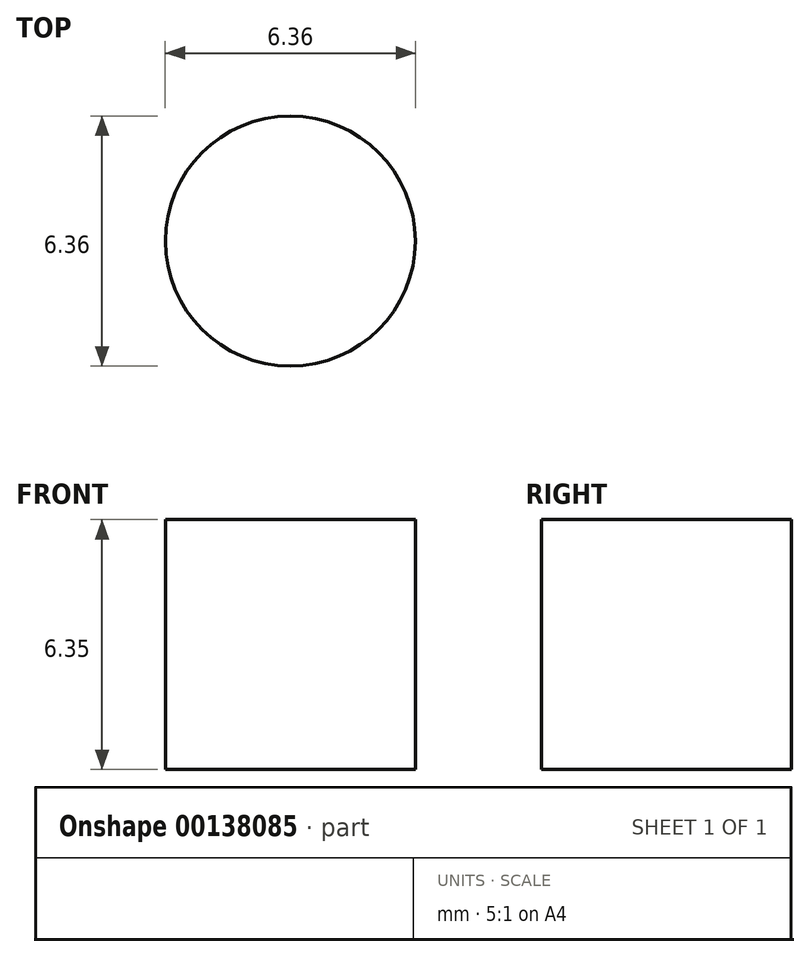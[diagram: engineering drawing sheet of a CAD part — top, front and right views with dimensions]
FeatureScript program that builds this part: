
annotation { "Feature Type Name" : "Feature", "Feature Type Description" : "" }
export const myFeature = defineFeature(function(context is Context, id is Id, definition is map)
    precondition{}
    {
        {
            var Q0;
            Q0=qCreatedBy(makeId("Top.planeOp"),FACE);
            var sketch = newSketch(context, id + "F0", { "sketchPlane" : qUnion([Q0])});
            skCircle(sketch, "E0", {"center": v(0, 0) * mm, "radius": 3.18 * mm});
            skSolve(sketch);
        }
        {
            var Q0;
            Q0 = qSketchRegion(id + "F0", true);
            extrude(context, id + "F1", {"entities" : qUnion([Q0]), "depth" : 6.35 * mm});
        }
    });
